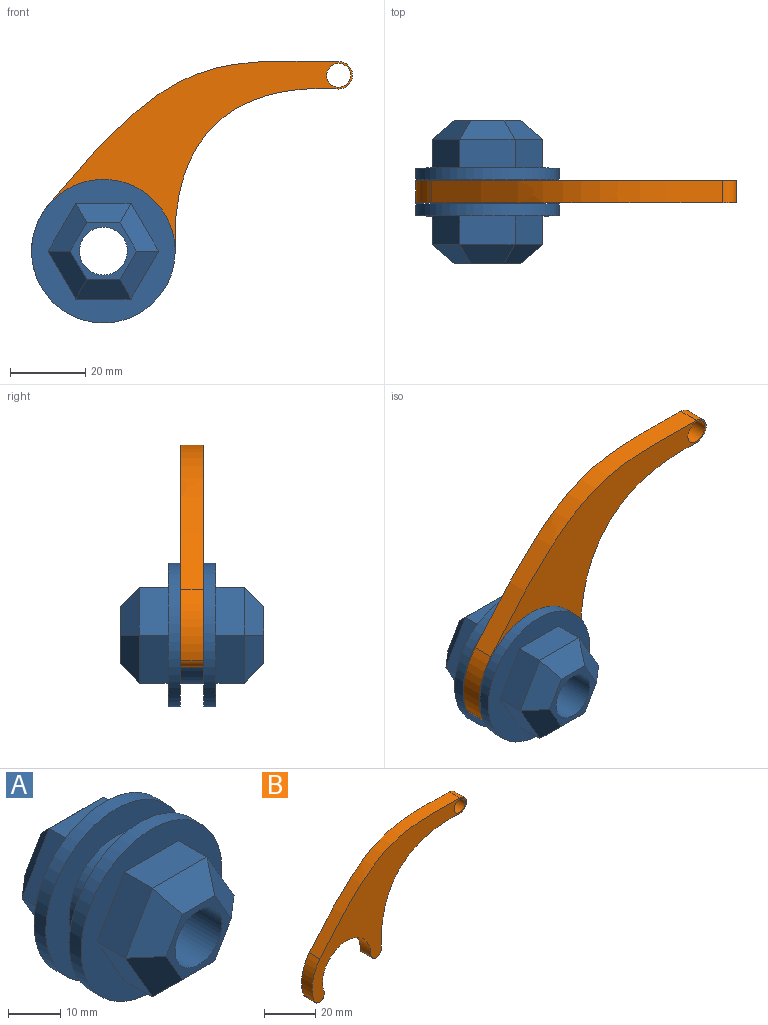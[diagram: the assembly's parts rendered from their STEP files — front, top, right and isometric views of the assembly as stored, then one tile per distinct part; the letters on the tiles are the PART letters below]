
ASSEMBLY  parts=2 mates=1
PART A: 34 faces, bbox 38.1x38.1x38.1 mm
  f0: plane 38.1x38.1mm, normal (0,1,0), area 581.4mm2, adj f2,f8,f9,f10,f11,f12,f13
  f1: cylinder r=12.7mm len=25.4mm, axis (0,1,0), area 506.7mm2, adj f3,f5
  f2: cylinder r=19.05mm len=38.1mm, axis (0,1,0), area 380mm2, adj f0,f3
  f3: plane 38.1x38.1mm, normal (0,-1,0), area 633.4mm2, adj f1,f2
  f4: cylinder r=19.05mm len=38.1mm, axis (0,-1,0), area 380mm2, adj f5,f6
  f5: plane 38.1x38.1mm, normal (0,1,0), area 633.4mm2, adj f1,f4
  f6: plane 38.1x38.1mm, normal (0,-1,0), area 581.4mm2, adj f4,f14,f15,f16,f17,f18,f19
  f7: plane 17.6x15.24mm, normal (0,-1,0), area 74.5mm2, adj f27,f28,f29,f30,f31,f32,f33
  f8: plane 12.7x7.62mm, normal (-0.87,0,0.5), area 111.7mm2, adj f0,f9,f13,f21
  f9: plane 14.66x7.62mm, normal (0,0,1), area 111.7mm2, adj f0,f8,f10,f22
  f10: plane 12.7x7.62mm, normal (0.87,0,0.5), area 111.7mm2, adj f0,f9,f11,f24
  f11: plane 12.7x7.62mm, normal (0.87,0,-0.5), area 111.7mm2, adj f0,f10,f12,f26
  f12: plane 14.66x7.62mm, normal (0,0,-1), area 111.7mm2, adj f0,f11,f13,f25
  f13: plane 12.7x7.62mm, normal (-0.87,0,-0.5), area 111.7mm2, adj f0,f8,f12,f23
  f14: plane 12.7x7.62mm, normal (0.87,0,0.5), area 111.7mm2, adj f6,f15,f19,f32
  f15: plane 14.66x7.62mm, normal (0,0,1), area 111.7mm2, adj f6,f14,f16,f31
  f16: plane 12.7x7.62mm, normal (-0.87,0,0.5), area 111.7mm2, adj f6,f15,f17,f29
  f17: plane 12.7x7.62mm, normal (-0.87,0,-0.5), area 111.7mm2, adj f6,f16,f18,f27
  f18: plane 14.66x7.62mm, normal (0,0,-1), area 111.7mm2, adj f6,f17,f19,f28
  f19: plane 12.7x7.62mm, normal (0.87,0,-0.5), area 111.7mm2, adj f6,f14,f18,f30
  f20: plane 17.6x15.24mm, normal (0,1,0), area 74.5mm2, adj f21,f22,f23,f24,f25,f26,f33
  f21: plane 12.7x10.27mm, normal (-0.61,0.71,0.35), area 84.3mm2, adj f8,f20,f22,f23
  f22: plane 14.66x5.08mm, normal (0,0.71,0.71), area 84.3mm2, adj f9,f20,f21,f24
  f23: plane 12.7x10.27mm, normal (-0.61,0.71,-0.35), area 84.3mm2, adj f13,f20,f21,f25
  f24: plane 12.7x10.27mm, normal (0.61,0.71,0.35), area 84.3mm2, adj f10,f20,f22,f26
  f25: plane 14.66x5.08mm, normal (0,0.71,-0.71), area 84.3mm2, adj f12,f20,f23,f26
  f26: plane 12.7x10.27mm, normal (0.61,0.71,-0.35), area 84.3mm2, adj f11,f20,f24,f25
  f27: plane 12.7x10.27mm, normal (-0.61,-0.71,-0.35), area 84.3mm2, adj f7,f17,f28,f29
  f28: plane 14.66x5.08mm, normal (0,-0.71,-0.71), area 84.3mm2, adj f7,f18,f27,f30
  f29: plane 12.7x10.27mm, normal (-0.61,-0.71,0.35), area 84.3mm2, adj f7,f16,f27,f31
  f30: plane 12.7x10.27mm, normal (0.61,-0.71,-0.35), area 84.3mm2, adj f7,f19,f28,f32
  f31: plane 14.66x5.08mm, normal (0,-0.71,0.71), area 84.3mm2, adj f7,f15,f29,f32
  f32: plane 12.7x10.27mm, normal (0.61,-0.71,0.35), area 84.3mm2, adj f7,f14,f30,f31
  f33: cylinder r=6.35mm len=38.1mm, axis (0,-1,0), area 1520.1mm2, adj f7,f20
PART B: 12 faces, bbox 85.1x5.8x60.4 mm
  f0: extruded ~5.84x1.3mm, area 7.6mm2, adj f1,f8,f10,f11
  f1: extruded ~43x41.83mm, area 407.1mm2, adj f0,f2,f10,f11
  f2: extruded ~5.84x0.43mm, area 2.5mm2, adj f1,f3,f10,f11
  f3: cylinder r=3.66mm len=7.31mm, axis (0,1,0), area 67.1mm2, adj f2,f4,f10,f11
  f4: extruded ~77.16x38.4mm, area 533.5mm2, adj f3,f5,f10,f11
  f5: cylinder r=19.05mm len=18.68mm, axis (0,1,0), area 115.8mm2, adj f4,f6,f10,f11
  f6: cylinder r=2.86mm len=5.84mm, axis (0,1,0), area 52.4mm2, adj f5,f7,f10,f11
  f7: cylinder r=13.33mm len=26.67mm, axis (0,1,0), area 272.4mm2, adj f6,f8,f10,f11
  f8: cylinder r=2.86mm len=5.84mm, axis (0,1,0), area 52.4mm2, adj f0,f7,f10,f11
  f9: cylinder r=3.17mm len=6.35mm, axis (0,1,0), area 116.5mm2, adj f10,f11
  f10: plane 85.12x60.41mm, normal (0,-1,0), area 1352.5mm2, adj f0,f1,f2,f3,f4,f5,f6,f7
  f11: plane 85.12x60.41mm, normal (0,1,0), area 1352.5mm2, adj f0,f1,f2,f3,f4,f5,f6,f7
PLACE A t=(-43.5,-26.99,-12.79)mm fixed
PLACE B t=(-43.5,-55.82,-12.79)mm
MATE revolute B.f7 <-> A.f33  axis (0,-1,0) through (-43.5,-61.66,-12.79)mm
